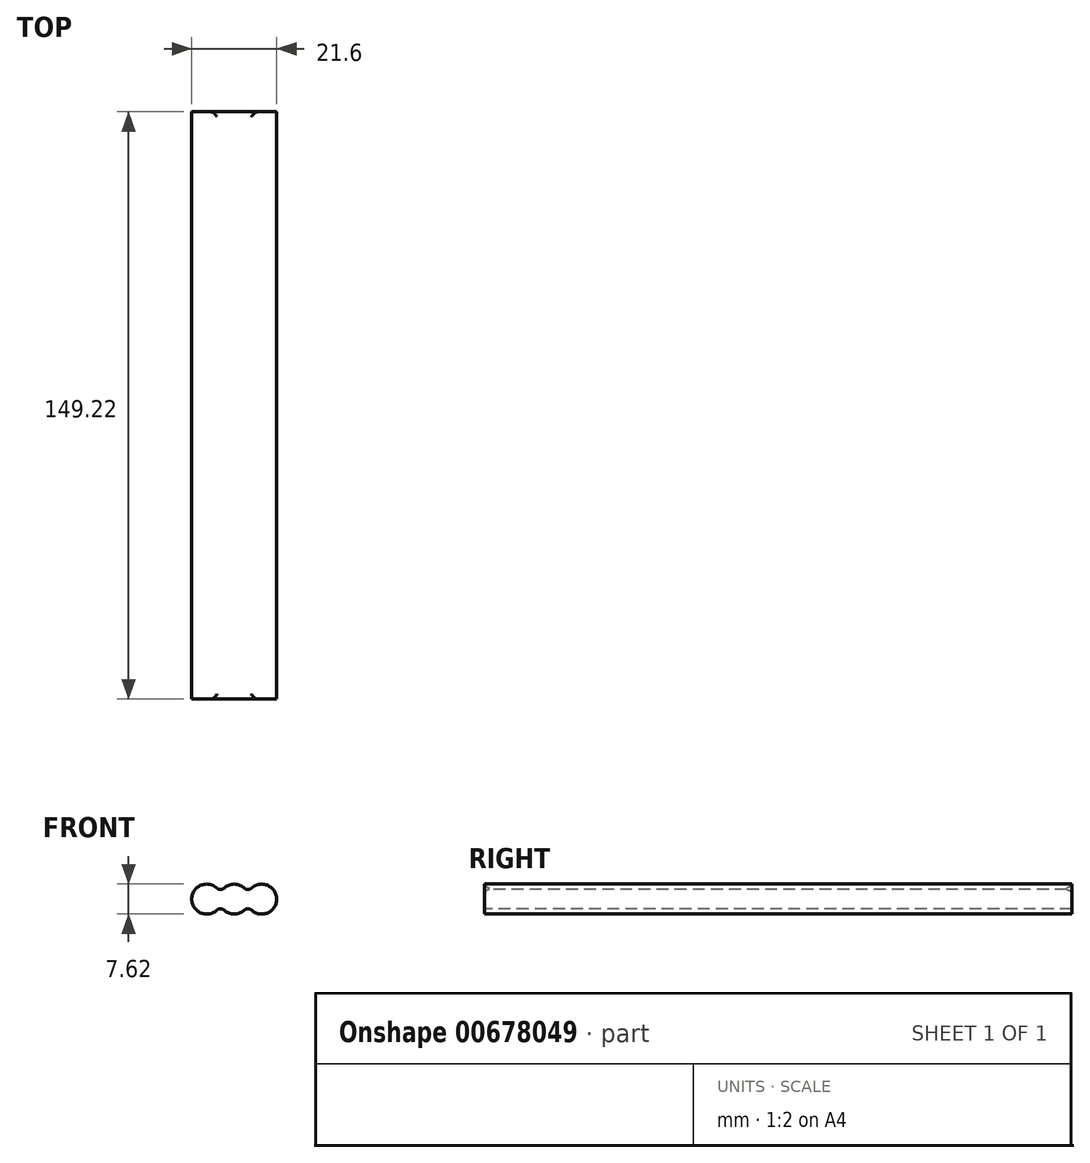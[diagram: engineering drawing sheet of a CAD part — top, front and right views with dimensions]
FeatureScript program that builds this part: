
annotation { "Feature Type Name" : "Feature", "Feature Type Description" : "" }
export const myFeature = defineFeature(function(context is Context, id is Id, definition is map)
    precondition{}
    {
        {
            var Q0;
            Q0=qCreatedBy(makeId("Front.planeOp"),FACE);
            var sketch = newSketch(context, id + "F0", { "sketchPlane" : qUnion([Q0])});
            skLineSegment(sketch, "E0", {"start": v(-6.99, 0) * mm, "end": v(6.99, 0) * mm, "construction": true});
            skPoint(sketch, "E1", {"position": v(0, 0) * mm});
            skArc(sketch, "E2", {"start": v(-3.5, 1.52) * mm, "mid": v(-10.8, 0) * mm, "end": v(-3.5, -1.52) * mm});
            skArc(sketch, "E3", {"start": v(3.5, 1.52) * mm, "mid": v(0, 3.81) * mm, "end": v(-3.5, 1.52) * mm});
            skArc(sketch, "E4", {"start": v(3.5, -1.52) * mm, "mid": v(10.8, 0) * mm, "end": v(3.5, 1.52) * mm});
            skArc(sketch, "E5.trimOffspring", {"start": v(-3.5, -1.52) * mm, "mid": v(0, -3.81) * mm, "end": v(3.5, -1.52) * mm});
            skSolve(sketch);
        }
        {
            var Q0;
            Q0=makeQuery(id+"F0.imprint","IMPRINT",FACE,{"disambiguationData":[TD([[makeQuery(id+"F0.imprint","IMPRINT",EDGE,{"derivedFrom":sQuery(id+"F0.wireOp",EDGE,"E2")}),1.0]])]});
            extrude(context, id + "F1", {"entities" : qUnion([Q0]), "depth" : 149.22 * mm, "offsetDistance" : 25.4 * mm, "symmetric" : true});
        }
        {
            var Q0;
            Q0=makeQuery(id+"F1.opExtrude","SWEPT_EDGE",EDGE,{"disambiguationData":[OSD([sQuery(id+"F0.wireOp",EDGE,"E3"),sQuery(id+"F0.wireOp",EDGE,"E4")])]});
            var Q1;
            Q1=makeQuery(id+"F1.opExtrude","SWEPT_EDGE",EDGE,{"disambiguationData":[OSD([sQuery(id+"F0.wireOp",EDGE,"E2"),sQuery(id+"F0.wireOp",EDGE,"E3")])]});
            var Q2;
            Q2=makeQuery(id+"F1.opExtrude","SWEPT_EDGE",EDGE,{"disambiguationData":[OSD([sQuery(id+"F0.wireOp",EDGE,"E2"),sQuery(id+"F0.wireOp",EDGE,"E5.trimOffspring")])]});
            var Q3;
            Q3=makeQuery(id+"F1.opExtrude","SWEPT_EDGE",EDGE,{"disambiguationData":[OSD([sQuery(id+"F0.wireOp",EDGE,"E4"),sQuery(id+"F0.wireOp",EDGE,"E5.trimOffspring")])]});
            var Q4;
            Q4=makeQuery(id+"F1.opExtrude","CAP_EDGE",EDGE,{"disambiguationData":[OSD([sQuery(id+"F0.wireOp",EDGE,"E3")])],"isStart":false});
            var Q5;
            Q5=makeQuery(id+"F1.opExtrude","CAP_EDGE",EDGE,{"disambiguationData":[OSD([sQuery(id+"F0.wireOp",EDGE,"E3")])],"isStart":true});
            fillet(context, id + "F2", {"entities" : qUnion([Q0, Q1, Q2, Q3, Q4, Q5]), "radius" : 1.27 * mm, "tangentPropagation" : true, "allowEdgeOverflow" : false});
        }
    });
